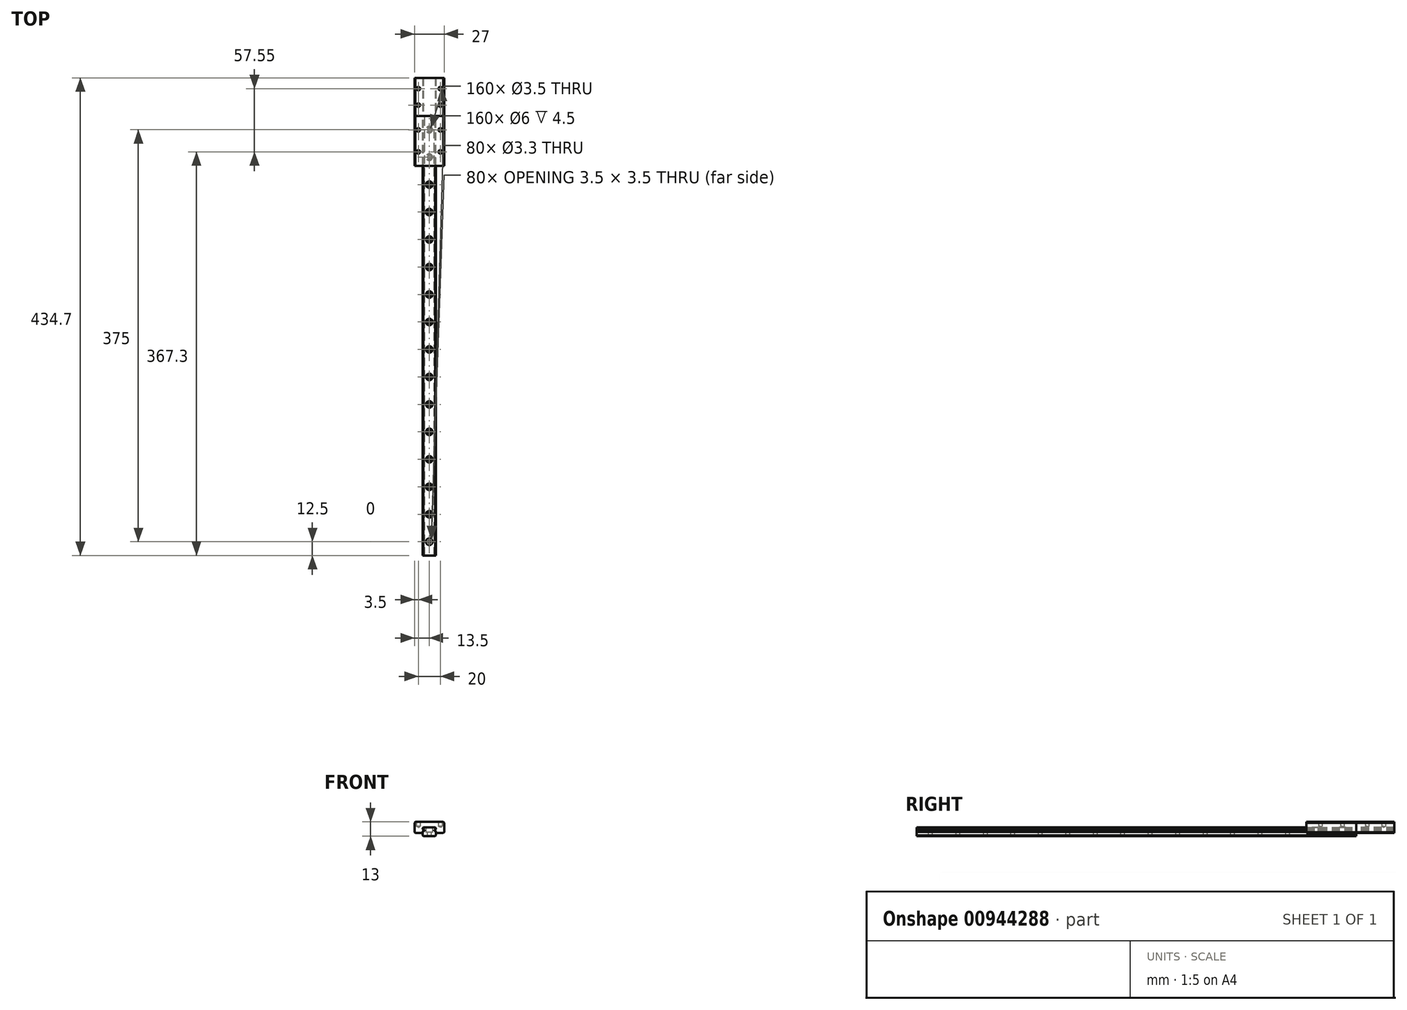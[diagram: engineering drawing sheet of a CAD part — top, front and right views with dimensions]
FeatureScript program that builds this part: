
annotation { "Feature Type Name" : "Feature", "Feature Type Description" : "" }
export const myFeature = defineFeature(function(context is Context, id is Id, definition is map)
    precondition{}
    {
        {
            var Q0;
            Q0=qCreatedBy(makeId("Front.planeOp"),FACE);
            var sketch = newSketch(context, id + "F0", { "sketchPlane" : qUnion([Q0])});
            skLineSegment(sketch, "E0.bottom", {"start": v(5.3, -4) * mm, "end": v(-5.3, -4) * mm});
            skLineSegment(sketch, "E0.top", {"start": v(5.3, 4) * mm, "end": v(-5.3, 4) * mm});
            skLineSegment(sketch, "E0.left", {"start": v(6, -3.3) * mm, "end": v(6, 0.09) * mm});
            skLineSegment(sketch, "E0.right", {"start": v(-6, -3.3) * mm, "end": v(-6, 0.09) * mm});
            skPoint(sketch, "E0.middle", {"position": v(0, 0) * mm});
            skLineSegment(sketch, "E1", {"start": v(0, 12.36) * mm, "end": v(0, -9.73) * mm, "construction": true});
            skLineSegment(sketch, "E2", {"start": v(-6, 2.5) * mm, "end": v(-5.3, 1.8) * mm});
            skLineSegment(sketch, "E3", {"start": v(-5.3, 1.8) * mm, "end": v(-4.3, 1.8) * mm});
            skLineSegment(sketch, "E4", {"start": v(-4.3, 1.8) * mm, "end": v(-4.3, 0.8) * mm});
            skLineSegment(sketch, "E5", {"start": v(-4.3, 0.8) * mm, "end": v(-5.3, 0.8) * mm});
            skLineSegment(sketch, "E6", {"start": v(-5.3, 0.8) * mm, "end": v(-6, 0.09) * mm});
            skLineSegment(sketch, "E7.MirrorCS", {"start": v(4.3, 0.8) * mm, "end": v(5.3, 0.8) * mm});
            skLineSegment(sketch, "E8.MirrorCS", {"start": v(5.3, 0.8) * mm, "end": v(6, 0.09) * mm});
            skLineSegment(sketch, "E9.MirrorCS", {"start": v(4.3, 1.8) * mm, "end": v(4.3, 0.8) * mm});
            skLineSegment(sketch, "E10.MirrorCS", {"start": v(6, 2.5) * mm, "end": v(5.3, 1.8) * mm});
            skLineSegment(sketch, "E11.MirrorCS", {"start": v(5.3, 1.8) * mm, "end": v(4.3, 1.8) * mm});
            skLineSegment(sketch, "E12.trimOffspring", {"start": v(-6, 2.5) * mm, "end": v(-6, 3.3) * mm});
            skLineSegment(sketch, "E13.trimOffspring", {"start": v(6, 2.5) * mm, "end": v(6, 3.3) * mm});
            skLineSegment(sketch, "E14", {"start": v(-6, 3.3) * mm, "end": v(-5.3, 4) * mm});
            skLineSegment(sketch, "E15.MirrorCS", {"start": v(6, 3.3) * mm, "end": v(5.3, 4) * mm});
            skLineSegment(sketch, "E16.MirrorCS", {"start": v(-6, -3.3) * mm, "end": v(-5.3, -4) * mm});
            skLineSegment(sketch, "E17.MirrorCS", {"start": v(6, -3.3) * mm, "end": v(5.3, -4) * mm});
            skPoint(sketch, "E18.orphan", {"position": v(-6, 4) * mm});
            skPoint(sketch, "E19.orphan", {"position": v(6, 4) * mm});
            skPoint(sketch, "E20.orphan", {"position": v(6, -4) * mm});
            skPoint(sketch, "E21.orphan", {"position": v(-6, -4) * mm});
            skSolve(sketch);
        }
        {
            var Q0;
            Q0=makeQuery(id+"F0.imprint","IMPRINT",FACE,{"disambiguationData":[TD([[makeQuery(id+"F0.imprint","IMPRINT",EDGE,{"derivedFrom":sQuery(id+"F0.wireOp",EDGE,"E0.bottom")}),-1.0]])]});
            extrude(context, id + "F1", {"entities" : qUnion([Q0]), "depth" : 400 * mm, "offsetDistance" : 25 * mm});
        }
        {
            var Q0;
            Q0=makeQuery(id+"F1.opExtrude","SWEPT_FACE",FACE,{"disambiguationData":[OSD([sQuery(id+"F0.wireOp",EDGE,"E0.top")])]});
            var sketch = newSketch(context, id + "F2", { "sketchPlane" : qUnion([Q0])});
            skLineSegment(sketch, "E22", {"start": v(0, 4.61) * mm, "end": v(0, -375.08) * mm, "construction": true});
            skCircle(sketch, "E23", {"center": v(0, -12.5) * mm, "radius": 1.75 * mm});
            skCircle(sketch, "E24.1.0.0", {"center": v(0, -37.5) * mm, "radius": 1.75 * mm});
            skCircle(sketch, "E24.2.0.0", {"center": v(0, -62.5) * mm, "radius": 1.75 * mm});
            skCircle(sketch, "E24.3.0.0", {"center": v(0, -87.5) * mm, "radius": 1.75 * mm});
            skCircle(sketch, "E24.4.0.0", {"center": v(0, -112.5) * mm, "radius": 1.75 * mm});
            skCircle(sketch, "E24.5.0.0", {"center": v(0, -137.5) * mm, "radius": 1.75 * mm});
            skCircle(sketch, "E24.6.0.0", {"center": v(0, -162.5) * mm, "radius": 1.75 * mm});
            skCircle(sketch, "E24.7.0.0", {"center": v(0, -187.5) * mm, "radius": 1.75 * mm});
            skCircle(sketch, "E24.8.0.0", {"center": v(0, -212.5) * mm, "radius": 1.75 * mm});
            skLineSegment(sketch, "E24.direction1", {"start": v(0, -12.5) * mm, "end": v(0, -37.5) * mm, "construction": true});
            skCircle(sketch, "E25.0.9.0", {"center": v(0, -237.5) * mm, "radius": 1.75 * mm});
            skCircle(sketch, "E25.0.10.0", {"center": v(0, -262.5) * mm, "radius": 1.75 * mm});
            skCircle(sketch, "E25.0.11.0", {"center": v(0, -287.5) * mm, "radius": 1.75 * mm});
            skCircle(sketch, "E25.0.12.0", {"center": v(0, -312.5) * mm, "radius": 1.75 * mm});
            skCircle(sketch, "E25.0.13.0", {"center": v(0, -337.5) * mm, "radius": 1.75 * mm});
            skCircle(sketch, "E26.0.14.0", {"center": v(0, -362.5) * mm, "radius": 1.75 * mm});
            skCircle(sketch, "E26.0.15.0", {"center": v(0, -387.5) * mm, "radius": 1.75 * mm});
            skSolve(sketch);
        }
        {
            var Q0;
            Q0=qSketchRegion(id+"F2",true);
            extrude(context, id + "F3", {"entities" : qUnion([Q0]), "operationType" : NewBodyOperationType.REMOVE, "endBound" : BoundingType.THROUGH_ALL, "oppositeDirection" : true, "depth" : 25 * mm, "offsetDistance" : 25 * mm});
        }
        {
            var Q0;
            Q0=makeQuery(id+"F1.opExtrude","SWEPT_FACE",FACE,{"disambiguationData":[OSD([sQuery(id+"F0.wireOp",EDGE,"E0.top")])]});
            var sketch = newSketch(context, id + "F4", { "sketchPlane" : qUnion([Q0])});
            skLineSegment(sketch, "E27", {"start": v(0, 167.82) * mm, "end": v(0, -211.88) * mm, "construction": true});
            skCircle(sketch, "E28", {"center": v(0, -12.5) * mm, "radius": 3 * mm});
            skCircle(sketch, "E29.1.0.0", {"center": v(0, -37.5) * mm, "radius": 3 * mm});
            skCircle(sketch, "E29.2.0.0", {"center": v(0, -62.5) * mm, "radius": 3 * mm});
            skCircle(sketch, "E29.3.0.0", {"center": v(0, -87.5) * mm, "radius": 3 * mm});
            skCircle(sketch, "E29.4.0.0", {"center": v(0, -112.5) * mm, "radius": 3 * mm});
            skCircle(sketch, "E29.5.0.0", {"center": v(0, -137.5) * mm, "radius": 3 * mm});
            skCircle(sketch, "E29.6.0.0", {"center": v(0, -162.5) * mm, "radius": 3 * mm});
            skCircle(sketch, "E29.7.0.0", {"center": v(0, -187.5) * mm, "radius": 3 * mm});
            skCircle(sketch, "E29.8.0.0", {"center": v(0, -212.5) * mm, "radius": 3 * mm});
            skLineSegment(sketch, "E29.direction1", {"start": v(0, -12.5) * mm, "end": v(0, -37.5) * mm, "construction": true});
            skCircle(sketch, "E30.0.9.0", {"center": v(0, -237.5) * mm, "radius": 3 * mm});
            skCircle(sketch, "E30.0.10.0", {"center": v(0, -262.5) * mm, "radius": 3 * mm});
            skCircle(sketch, "E30.0.11.0", {"center": v(0, -287.5) * mm, "radius": 3 * mm});
            skCircle(sketch, "E30.0.12.0", {"center": v(0, -312.5) * mm, "radius": 3 * mm});
            skCircle(sketch, "E30.0.13.0", {"center": v(0, -337.5) * mm, "radius": 3 * mm});
            skCircle(sketch, "E31.0.14.0", {"center": v(0, -362.5) * mm, "radius": 3 * mm});
            skCircle(sketch, "E31.0.15.0", {"center": v(0, -387.5) * mm, "radius": 3 * mm});
            skSolve(sketch);
        }
        {
            var Q0;
            Q0=qSketchRegion(id+"F4",true);
            extrude(context, id + "F5", {"entities" : qUnion([Q0]), "operationType" : NewBodyOperationType.REMOVE, "oppositeDirection" : true, "depth" : 4.5 * mm, "offsetDistance" : 25 * mm});
        }
        {
            var Q0;
            Q0=qCreatedBy(makeId("Front.planeOp"),FACE);
            var sketch = newSketch(context, id + "F6", { "sketchPlane" : qUnion([Q0])});
            skLineSegment(sketch, "E32", {"start": v(-6.15, -1) * mm, "end": v(-12.8, -1) * mm});
            skLineSegment(sketch, "E33", {"start": v(-13.5, -0.3) * mm, "end": v(-13.5, 8.3) * mm});
            skLineSegment(sketch, "E34", {"start": v(-12.8, 9) * mm, "end": v(0, 9) * mm});
            skLineSegment(sketch, "E35", {"start": v(-6.15, -1) * mm, "end": v(-6.15, 0.15) * mm});
            skLineSegment(sketch, "E36", {"start": v(-6.15, 0.15) * mm, "end": v(-5.3, 1) * mm});
            skLineSegment(sketch, "E37", {"start": v(-5.3, 1) * mm, "end": v(-5.3, 1.58) * mm});
            skLineSegment(sketch, "E38", {"start": v(-5.3, 1.58) * mm, "end": v(-6.15, 2.44) * mm});
            skLineSegment(sketch, "E39", {"start": v(-6.15, 2.44) * mm, "end": v(-6.15, 3.36) * mm});
            skLineSegment(sketch, "E40", {"start": v(-6.15, 3.36) * mm, "end": v(-5.36, 4.15) * mm});
            skLineSegment(sketch, "E41", {"start": v(-5.36, 4.15) * mm, "end": v(0, 4.15) * mm});
            skLineSegment(sketch, "E42", {"start": v(-13.5, 8.3) * mm, "end": v(-12.8, 9) * mm});
            skLineSegment(sketch, "E43", {"start": v(-12.8, -1) * mm, "end": v(-13.5, -0.3) * mm});
            skPoint(sketch, "E44.orphan", {"position": v(-13.5, -1) * mm});
            skPoint(sketch, "E45.orphan", {"position": v(-13.5, 9) * mm});
            skLineSegment(sketch, "E46.MirrorCS", {"start": v(12.8, 9) * mm, "end": v(0, 9) * mm});
            skLineSegment(sketch, "E47.MirrorCS", {"start": v(13.5, 8.3) * mm, "end": v(12.8, 9) * mm});
            skLineSegment(sketch, "E48.MirrorCS", {"start": v(13.5, -0.3) * mm, "end": v(13.5, 8.3) * mm});
            skLineSegment(sketch, "E49.MirrorCS", {"start": v(12.8, -1) * mm, "end": v(13.5, -0.3) * mm});
            skLineSegment(sketch, "E50.MirrorCS", {"start": v(6.15, -1) * mm, "end": v(12.8, -1) * mm});
            skLineSegment(sketch, "E51.MirrorCS", {"start": v(6.15, -1) * mm, "end": v(6.15, 0.15) * mm});
            skLineSegment(sketch, "E52.MirrorCS", {"start": v(6.15, 0.15) * mm, "end": v(5.3, 1) * mm});
            skLineSegment(sketch, "E53.MirrorCS", {"start": v(5.3, 1) * mm, "end": v(5.3, 1.58) * mm});
            skLineSegment(sketch, "E54.MirrorCS", {"start": v(5.3, 1.58) * mm, "end": v(6.15, 2.44) * mm});
            skLineSegment(sketch, "E55.MirrorCS", {"start": v(6.15, 2.44) * mm, "end": v(6.15, 3.36) * mm});
            skLineSegment(sketch, "E56.MirrorCS", {"start": v(6.15, 3.36) * mm, "end": v(5.36, 4.15) * mm});
            skLineSegment(sketch, "E57.MirrorCS", {"start": v(5.36, 4.15) * mm, "end": v(0, 4.15) * mm});
            skSolve(sketch);
        }
        {
            var Q0;
            Q0=qSketchRegion(id+"F6",true);
            extrude(context, id + "F7", {"entities" : qUnion([Q0]), "depth" : 45.4 * mm, "offsetDistance" : 25 * mm});
        }
        {
            var Q0;
            Q0=qSketchRegion(id+"F6",true);
            extrude(context, id + "F8", {"entities" : qUnion([Q0]), "oppositeDirection" : true, "depth" : 34.7 * mm, "offsetDistance" : 25 * mm});
        }
        {
            var Q0;
            Q0=makeQuery(id+"F7.opExtrude","SWEPT_FACE",FACE,{"disambiguationData":[OSD([sQuery(id+"F6.wireOp",EDGE,"E34"),sQuery(id+"F6.wireOp",EDGE,"E46.MirrorCS")])]});
            var sketch = newSketch(context, id + "F9", { "sketchPlane" : qUnion([Q0])});
            skLineSegment(sketch, "E58", {"start": v(-12.8, 0) * mm, "end": v(12.8, -45.4) * mm, "construction": true});
            skLineSegment(sketch, "E59", {"start": v(12.8, 0) * mm, "end": v(-12.8, -45.4) * mm, "construction": true});
            skLineSegment(sketch, "E60", {"start": v(-37.81, -22.7) * mm, "end": v(32.35, -22.7) * mm, "construction": true});
            skPoint(sketch, "E60.startSnap0", {"position": v(0, -22.7) * mm});
            skLineSegment(sketch, "E61", {"start": v(0, 0) * mm, "end": v(0, -61.52) * mm, "construction": true});
            skCircle(sketch, "E62", {"center": v(-10, -12.7) * mm, "radius": 1.5 * mm});
            skCircle(sketch, "E63.MirrorC", {"center": v(10, -12.7) * mm, "radius": 1.5 * mm});
            skCircle(sketch, "E64.MirrorC", {"center": v(-10, -32.7) * mm, "radius": 1.5 * mm});
            skCircle(sketch, "E65.MirrorC", {"center": v(10, -32.7) * mm, "radius": 1.5 * mm});
            skSolve(sketch);
        }
        {
            var Q0;
            Q0=makeQuery(id+"F8.opExtrude","SWEPT_FACE",FACE,{"disambiguationData":[OSD([sQuery(id+"F6.wireOp",EDGE,"E34"),sQuery(id+"F6.wireOp",EDGE,"E46.MirrorCS")])]});
            var sketch = newSketch(context, id + "F10", { "sketchPlane" : qUnion([Q0])});
            skLineSegment(sketch, "E66", {"start": v(-34.35, 17.35) * mm, "end": v(28.23, 17.35) * mm, "construction": true});
            skLineSegment(sketch, "E67", {"start": v(0, 49.38) * mm, "end": v(0, -1.77) * mm, "construction": true});
            skCircle(sketch, "E68", {"center": v(-10, 24.85) * mm, "radius": 1.5 * mm});
            skCircle(sketch, "E69.MirrorC", {"center": v(10, 24.85) * mm, "radius": 1.5 * mm});
            skCircle(sketch, "E70.MirrorC", {"center": v(-10, 9.85) * mm, "radius": 1.5 * mm});
            skCircle(sketch, "E71.MirrorC", {"center": v(10, 9.85) * mm, "radius": 1.5 * mm});
            skSolve(sketch);
        }
        {
            var Q0;
            Q0=sQuery(id+"F9.wireOp",VERTEX,"E62.center");
            var Q1;
            Q1=sQuery(id+"F9.wireOp",VERTEX,"E63.MirrorC.center");
            var Q2;
            Q2=sQuery(id+"F9.wireOp",VERTEX,"E64.MirrorC.center");
            var Q3;
            Q3=sQuery(id+"F9.wireOp",VERTEX,"E65.MirrorC.center");
            var Q4;
            Q4=makeQuery(id+"F7.opExtrude","SWEPT_BODY",BODY,{"disambiguationData":[OSD([sQuery(id+"F6.wireOp",EDGE,"E32"),sQuery(id+"F6.wireOp",EDGE,"E33"),sQuery(id+"F6.wireOp",EDGE,"E34"),sQuery(id+"F6.wireOp",EDGE,"E35"),sQuery(id+"F6.wireOp",EDGE,"E36"),sQuery(id+"F6.wireOp",EDGE,"E37"),sQuery(id+"F6.wireOp",EDGE,"E38"),sQuery(id+"F6.wireOp",EDGE,"E39"),sQuery(id+"F6.wireOp",EDGE,"E40"),sQuery(id+"F6.wireOp",EDGE,"E41"),sQuery(id+"F6.wireOp",EDGE,"E42"),sQuery(id+"F6.wireOp",EDGE,"E43"),sQuery(id+"F6.wireOp",EDGE,"E46.MirrorCS"),sQuery(id+"F6.wireOp",EDGE,"E47.MirrorCS"),sQuery(id+"F6.wireOp",EDGE,"E48.MirrorCS"),sQuery(id+"F6.wireOp",EDGE,"E49.MirrorCS"),sQuery(id+"F6.wireOp",EDGE,"E50.MirrorCS"),sQuery(id+"F6.wireOp",EDGE,"E51.MirrorCS"),sQuery(id+"F6.wireOp",EDGE,"E52.MirrorCS"),sQuery(id+"F6.wireOp",EDGE,"E53.MirrorCS"),sQuery(id+"F6.wireOp",EDGE,"E54.MirrorCS"),sQuery(id+"F6.wireOp",EDGE,"E55.MirrorCS"),sQuery(id+"F6.wireOp",EDGE,"E56.MirrorCS"),sQuery(id+"F6.wireOp",EDGE,"E57.MirrorCS")])]});
            hole(context, id + "F11", {"style" : HoleStyle.SIMPLE, "endStyle" : HoleEndStyle.BLIND, "standardTappedOrClearance" : lookupTablePath({ "standard" : "ISO", "fit" : "Normal", "size" : "M3", "type" : "Clearance" }), "standardBlindInLast" : lookupTablePath({ "fit" : "Standard", "standard" : "ISO", "size" : "M3", "type" : "Clearance" }), "holeDiameter" : 3.3 * mm, "majorDiameter" : 5 * mm, "holeDepth" : 4 * mm, "isTappedThrough" : true, "tappedDepth" : 12 * mm, "tapClearance" : 3, "locations" : qUnion([Q0, Q1, Q2, Q3]), "scope" : qUnion([Q4]), "startStyle" : HoleStartStyle.SKETCH});
        }
        {
            var Q0;
            Q0=sQuery(id+"F10.wireOp",VERTEX,"E68.center");
            var Q1;
            Q1=sQuery(id+"F10.wireOp",VERTEX,"E69.MirrorC.center");
            var Q2;
            Q2=sQuery(id+"F10.wireOp",VERTEX,"E71.MirrorC.center");
            var Q3;
            Q3=sQuery(id+"F10.wireOp",VERTEX,"E70.MirrorC.center");
            var Q4;
            Q4=makeQuery(id+"F8.opExtrude","SWEPT_BODY",BODY,{"disambiguationData":[OSD([sQuery(id+"F6.wireOp",EDGE,"E32"),sQuery(id+"F6.wireOp",EDGE,"E33"),sQuery(id+"F6.wireOp",EDGE,"E34"),sQuery(id+"F6.wireOp",EDGE,"E35"),sQuery(id+"F6.wireOp",EDGE,"E36"),sQuery(id+"F6.wireOp",EDGE,"E37"),sQuery(id+"F6.wireOp",EDGE,"E38"),sQuery(id+"F6.wireOp",EDGE,"E39"),sQuery(id+"F6.wireOp",EDGE,"E40"),sQuery(id+"F6.wireOp",EDGE,"E41"),sQuery(id+"F6.wireOp",EDGE,"E42"),sQuery(id+"F6.wireOp",EDGE,"E43"),sQuery(id+"F6.wireOp",EDGE,"E46.MirrorCS"),sQuery(id+"F6.wireOp",EDGE,"E47.MirrorCS"),sQuery(id+"F6.wireOp",EDGE,"E48.MirrorCS"),sQuery(id+"F6.wireOp",EDGE,"E49.MirrorCS"),sQuery(id+"F6.wireOp",EDGE,"E50.MirrorCS"),sQuery(id+"F6.wireOp",EDGE,"E51.MirrorCS"),sQuery(id+"F6.wireOp",EDGE,"E52.MirrorCS"),sQuery(id+"F6.wireOp",EDGE,"E53.MirrorCS"),sQuery(id+"F6.wireOp",EDGE,"E54.MirrorCS"),sQuery(id+"F6.wireOp",EDGE,"E55.MirrorCS"),sQuery(id+"F6.wireOp",EDGE,"E56.MirrorCS"),sQuery(id+"F6.wireOp",EDGE,"E57.MirrorCS")])]});
            hole(context, id + "F12", {"style" : HoleStyle.SIMPLE, "endStyle" : HoleEndStyle.BLIND, "standardTappedOrClearance" : lookupTablePath({ "standard" : "ISO", "fit" : "Normal", "size" : "M3", "type" : "Clearance" }), "standardBlindInLast" : lookupTablePath({ "fit" : "Standard", "standard" : "ISO", "size" : "M3", "type" : "Clearance" }), "holeDiameter" : 3.3 * mm, "majorDiameter" : 5 * mm, "holeDepth" : 4 * mm, "isTappedThrough" : true, "tappedDepth" : 12 * mm, "tapClearance" : 3, "locations" : qUnion([Q0, Q1, Q2, Q3]), "scope" : qUnion([Q4]), "startStyle" : HoleStartStyle.SKETCH});
        }
    });
